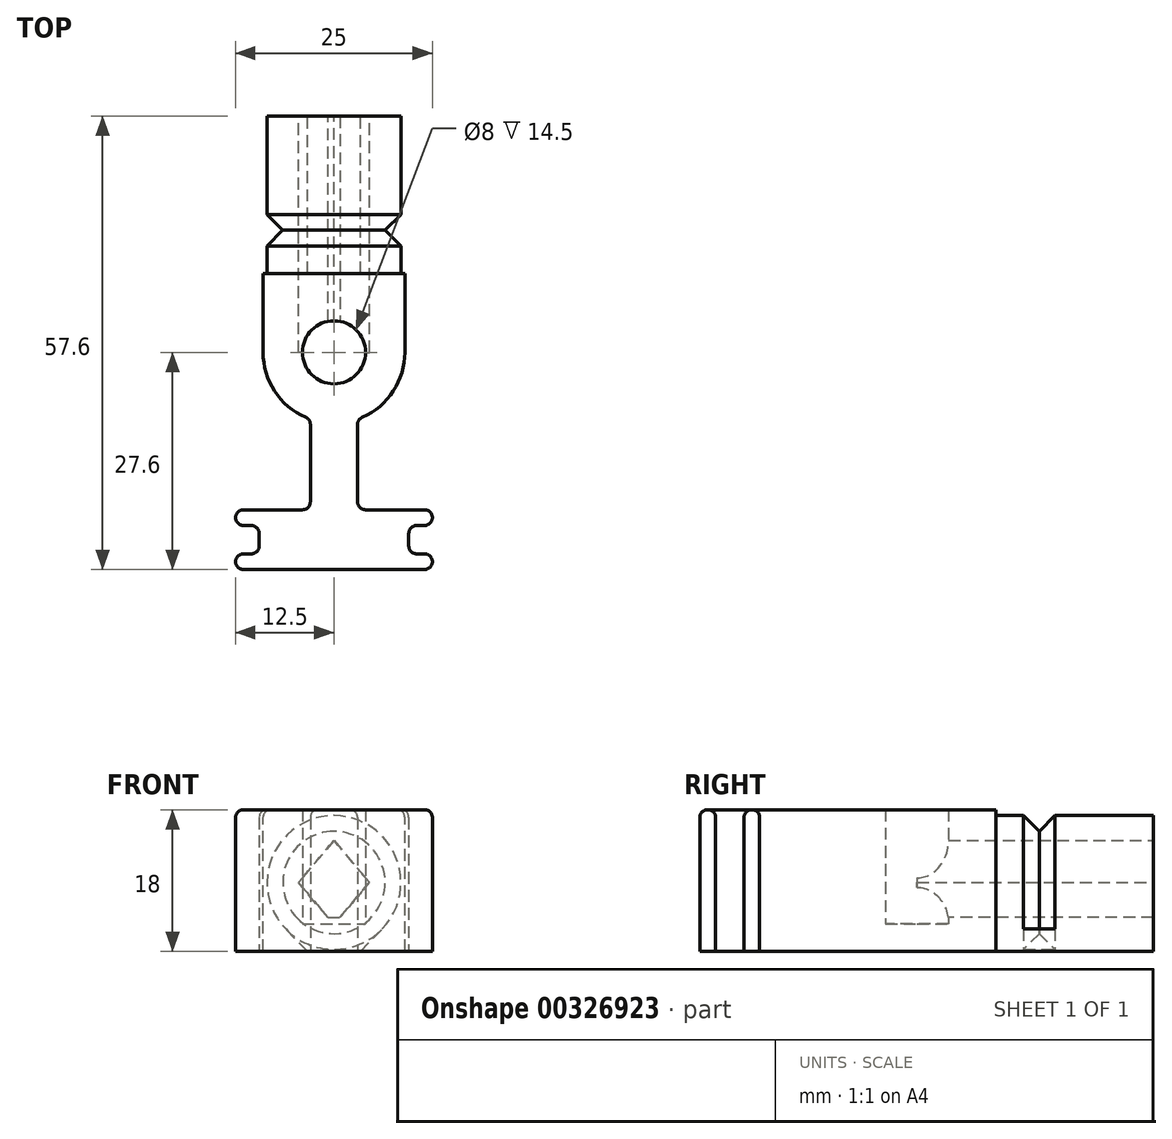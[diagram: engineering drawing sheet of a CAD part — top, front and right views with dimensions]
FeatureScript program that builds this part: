
annotation { "Feature Type Name" : "Feature", "Feature Type Description" : "" }
export const myFeature = defineFeature(function(context is Context, id is Id, definition is map)
    precondition{}
    {
        {
            var Q0;
            Q0=qCreatedBy(makeId("Top.planeOp"),FACE);
            var sketch = newSketch(context, id + "F0", { "sketchPlane" : qUnion([Q0])});
            skCircle(sketch, "E0", {"center": v(0, 0) * mm, "radius": 4 * mm});
            skArc(sketch, "E1", {"start": v(3, -8.49) * mm, "mid": v(7.35, -5.2) * mm, "end": v(9, 0) * mm});
            skLineSegment(sketch, "E2", {"start": v(-3, -8.49) * mm, "end": v(-3, -20) * mm});
            skLineSegment(sketch, "E3", {"start": v(-3, -20) * mm, "end": v(-12.5, -20) * mm});
            skLineSegment(sketch, "E4", {"start": v(-12.5, -20) * mm, "end": v(-12.5, -22) * mm});
            skLineSegment(sketch, "E5", {"start": v(-12.5, -22) * mm, "end": v(-9.5, -22) * mm});
            skLineSegment(sketch, "E6", {"start": v(-9.5, -22) * mm, "end": v(-9.5, -25.6) * mm});
            skLineSegment(sketch, "E7", {"start": v(-9.5, -25.6) * mm, "end": v(-12.5, -25.6) * mm});
            skLineSegment(sketch, "E8", {"start": v(-12.5, -25.6) * mm, "end": v(-12.5, -27.6) * mm});
            skLineSegment(sketch, "E9", {"start": v(-12.5, -27.6) * mm, "end": v(0, -27.6) * mm});
            skLineSegment(sketch, "E10", {"start": v(0, -27.6) * mm, "end": v(0, 0) * mm, "construction": true});
            skLineSegment(sketch, "E11.MirrorCS", {"start": v(3, -8.49) * mm, "end": v(3, -20) * mm});
            skLineSegment(sketch, "E12.MirrorCS", {"start": v(12.5, -25.6) * mm, "end": v(12.5, -27.6) * mm});
            skLineSegment(sketch, "E13.MirrorCS", {"start": v(12.5, -20) * mm, "end": v(12.5, -22) * mm});
            skLineSegment(sketch, "E14.MirrorCS", {"start": v(12.5, -27.6) * mm, "end": v(0, -27.6) * mm});
            skLineSegment(sketch, "E15.MirrorCS", {"start": v(3, -20) * mm, "end": v(12.5, -20) * mm});
            skLineSegment(sketch, "E16.MirrorCS", {"start": v(12.5, -22) * mm, "end": v(9.5, -22) * mm});
            skLineSegment(sketch, "E17.MirrorCS", {"start": v(9.5, -25.6) * mm, "end": v(12.5, -25.6) * mm});
            skLineSegment(sketch, "E18.MirrorCS", {"start": v(9.5, -22) * mm, "end": v(9.5, -25.6) * mm});
            skLineSegment(sketch, "E19", {"start": v(-9, 0) * mm, "end": v(-9, 30) * mm});
            skLineSegment(sketch, "E20", {"start": v(-9, 30) * mm, "end": v(9, 30) * mm});
            skLineSegment(sketch, "E21", {"start": v(9, 30) * mm, "end": v(9, 0) * mm});
            skArc(sketch, "E22.trimOffspring", {"start": v(-9, 0) * mm, "mid": v(-7.35, -5.2) * mm, "end": v(-3, -8.49) * mm});
            skSolve(sketch);
        }
        {
            var Q0;
            Q0=qSketchRegion(id+"F0",true);
            extrude(context, id + "F1", {"entities" : qUnion([Q0]), "depth" : 18 * mm});
        }
        {
            var Q0;
            Q0=makeQuery(id+"F1.opExtrude","CAP_FACE",FACE,{"disambiguationData":[OSD([sQuery(id+"F0.wireOp",EDGE,"E0"),sQuery(id+"F0.wireOp",EDGE,"E1"),sQuery(id+"F0.wireOp",EDGE,"E2"),sQuery(id+"F0.wireOp",EDGE,"E3"),sQuery(id+"F0.wireOp",EDGE,"E4"),sQuery(id+"F0.wireOp",EDGE,"E5"),sQuery(id+"F0.wireOp",EDGE,"E6"),sQuery(id+"F0.wireOp",EDGE,"E7"),sQuery(id+"F0.wireOp",EDGE,"E8"),sQuery(id+"F0.wireOp",EDGE,"E9"),sQuery(id+"F0.wireOp",EDGE,"E11.MirrorCS"),sQuery(id+"F0.wireOp",EDGE,"E12.MirrorCS"),sQuery(id+"F0.wireOp",EDGE,"E13.MirrorCS"),sQuery(id+"F0.wireOp",EDGE,"E14.MirrorCS"),sQuery(id+"F0.wireOp",EDGE,"E15.MirrorCS"),sQuery(id+"F0.wireOp",EDGE,"E16.MirrorCS"),sQuery(id+"F0.wireOp",EDGE,"E17.MirrorCS"),sQuery(id+"F0.wireOp",EDGE,"E18.MirrorCS")])],"isStart":false});
            var sketch = newSketch(context, id + "F2", { "sketchPlane" : qUnion([Q0])});
            skCircle(sketch, "E23.0", {"center": v(0, 0) * mm, "radius": 4 * mm});
            skCircle(sketch, "E24", {"center": v(0, 0) * mm, "radius": 9 * mm});
            skSolve(sketch);
        }
        {
            var Q0;
            Q0=makeQuery(id+"F1.opExtrude","SWEPT_EDGE",EDGE,{"disambiguationData":[OSD([sQuery(id+"F0.wireOp",EDGE,"E11.MirrorCS"),sQuery(id+"F0.wireOp",EDGE,"E15.MirrorCS")])]});
            var Q1;
            Q1=makeQuery(id+"F1.opExtrude","SWEPT_EDGE",EDGE,{"disambiguationData":[OSD([sQuery(id+"F0.wireOp",EDGE,"E2"),sQuery(id+"F0.wireOp",EDGE,"E3")])]});
            var Q2;
            Q2=makeQuery(id+"F1.opExtrude","SWEPT_EDGE",EDGE,{"disambiguationData":[OSD([sQuery(id+"F0.wireOp",EDGE,"E1"),sQuery(id+"F0.wireOp",EDGE,"E2")])]});
            var Q3;
            Q3=makeQuery(id+"F1.opExtrude","SWEPT_EDGE",EDGE,{"disambiguationData":[OSD([sQuery(id+"F0.wireOp",EDGE,"E1"),sQuery(id+"F0.wireOp",EDGE,"E11.MirrorCS")])]});
            var Q4;
            Q4=makeQuery(id+"F1.opExtrude","SWEPT_EDGE",EDGE,{"disambiguationData":[OSD([sQuery(id+"F0.wireOp",EDGE,"E12.MirrorCS"),sQuery(id+"F0.wireOp",EDGE,"E14.MirrorCS")])]});
            var Q5;
            Q5=makeQuery(id+"F1.opExtrude","SWEPT_EDGE",EDGE,{"disambiguationData":[OSD([sQuery(id+"F0.wireOp",EDGE,"E8"),sQuery(id+"F0.wireOp",EDGE,"E9")])]});
            var Q6;
            Q6=makeQuery(id+"F1.opExtrude","SWEPT_EDGE",EDGE,{"disambiguationData":[OSD([sQuery(id+"F0.wireOp",EDGE,"E6"),sQuery(id+"F0.wireOp",EDGE,"E7")])]});
            var Q7;
            Q7=makeQuery(id+"F1.opExtrude","SWEPT_EDGE",EDGE,{"disambiguationData":[OSD([sQuery(id+"F0.wireOp",EDGE,"E7"),sQuery(id+"F0.wireOp",EDGE,"E8")])]});
            var Q8;
            Q8=makeQuery(id+"F1.opExtrude","SWEPT_EDGE",EDGE,{"disambiguationData":[OSD([sQuery(id+"F0.wireOp",EDGE,"E5"),sQuery(id+"F0.wireOp",EDGE,"E6")])]});
            var Q9;
            Q9=makeQuery(id+"F1.opExtrude","SWEPT_EDGE",EDGE,{"disambiguationData":[OSD([sQuery(id+"F0.wireOp",EDGE,"E4"),sQuery(id+"F0.wireOp",EDGE,"E5")])]});
            var Q10;
            Q10=makeQuery(id+"F1.opExtrude","SWEPT_EDGE",EDGE,{"disambiguationData":[OSD([sQuery(id+"F0.wireOp",EDGE,"E3"),sQuery(id+"F0.wireOp",EDGE,"E4")])]});
            var Q11;
            Q11=makeQuery(id+"F1.opExtrude","SWEPT_EDGE",EDGE,{"disambiguationData":[OSD([sQuery(id+"F0.wireOp",EDGE,"E12.MirrorCS"),sQuery(id+"F0.wireOp",EDGE,"E17.MirrorCS")])]});
            var Q12;
            Q12=makeQuery(id+"F1.opExtrude","SWEPT_EDGE",EDGE,{"disambiguationData":[OSD([sQuery(id+"F0.wireOp",EDGE,"E17.MirrorCS"),sQuery(id+"F0.wireOp",EDGE,"E18.MirrorCS")])]});
            var Q13;
            Q13=makeQuery(id+"F1.opExtrude","SWEPT_EDGE",EDGE,{"disambiguationData":[OSD([sQuery(id+"F0.wireOp",EDGE,"E16.MirrorCS"),sQuery(id+"F0.wireOp",EDGE,"E18.MirrorCS")])]});
            var Q14;
            Q14=makeQuery(id+"F1.opExtrude","SWEPT_EDGE",EDGE,{"disambiguationData":[OSD([sQuery(id+"F0.wireOp",EDGE,"E13.MirrorCS"),sQuery(id+"F0.wireOp",EDGE,"E16.MirrorCS")])]});
            var Q15;
            Q15=makeQuery(id+"F1.opExtrude","SWEPT_EDGE",EDGE,{"disambiguationData":[OSD([sQuery(id+"F0.wireOp",EDGE,"E13.MirrorCS"),sQuery(id+"F0.wireOp",EDGE,"E15.MirrorCS")])]});
            fillet(context, id + "F3", {"entities" : qUnion([Q0, Q1, Q2, Q3, Q4, Q5, Q6, Q7, Q8, Q9, Q10, Q11, Q12, Q13, Q14, Q15]), "radius" : 1 * mm, "tangentPropagation" : true, "allowEdgeOverflow" : false});
        }
        {
            var Q0;
            Q0=makeQuery(id+"FmhpY0We5Ry6qRu_1.opFillet","BLEND_EDGE",EDGE,{"blendedFrom":[makeQuery(id+"FVQWmpm12YIfkNp_1.opExtrude","CAP_EDGE",EDGE,{"disambiguationData":[OSD([sQuery(id+"F2.wireOp",EDGE,"E24")])],"isStart":true}),makeQuery(id+"F1.opExtrude","SWEPT_FACE",FACE,{"disambiguationData":[OSD([sQuery(id+"F0.wireOp",EDGE,"E2")])]})],"blendedInto":[makeQuery(id+"F1.opExtrude","SWEPT_FACE",FACE,{"disambiguationData":[OSD([sQuery(id+"F0.wireOp",EDGE,"E2")])]})]});
            var Q1;
            Q1=makeQuery(id+"FmhpY0We5Ry6qRu_1.opFillet","BLEND_EDGE",EDGE,{"blendedFrom":[makeQuery(id+"FVQWmpm12YIfkNp_1.opExtrude","CAP_EDGE",EDGE,{"disambiguationData":[OSD([sQuery(id+"F2.wireOp",EDGE,"E24")])],"isStart":true}),makeQuery(id+"F3.opFillet","BLEND_FACE",FACE,{"disambiguationData":[OSD([sQuery(id+"F0.wireOp",EDGE,"E1"),sQuery(id+"F0.wireOp",EDGE,"E2")])]})],"blendedInto":[makeQuery(id+"F3.opFillet","BLEND_FACE",FACE,{"disambiguationData":[OSD([sQuery(id+"F0.wireOp",EDGE,"E1"),sQuery(id+"F0.wireOp",EDGE,"E2")])]})]});
            var Q2;
            Q2=makeQuery(id+"F1.opExtrude","CAP_EDGE",EDGE,{"disambiguationData":[OSD([sQuery(id+"F0.wireOp",EDGE,"E2")])],"isStart":false});
            fillet(context, id + "F4", {"entities" : qUnion([Q0, Q1, Q2]), "radius" : 1 * mm, "tangentPropagation" : true, "allowEdgeOverflow" : false});
        }
        {
            var Q0;
            Q0=makeQuery(id+"F1.opExtrude","SWEPT_FACE",FACE,{"disambiguationData":[OSD([sQuery(id+"F0.wireOp",EDGE,"E20")])]});
            var sketch = newSketch(context, id + "F5", { "sketchPlane" : qUnion([Q0])});
            skLineSegment(sketch, "E25", {"start": v(0, 0) * mm, "end": v(0, 27.76) * mm, "construction": true});
            skLineSegment(sketch, "E26", {"start": v(0, 0) * mm, "end": v(3.37, 0) * mm});
            skLineSegment(sketch, "E27", {"start": v(3.37, 0) * mm, "end": v(6.11, 2.84) * mm});
            skArc(sketch, "E28", {"start": v(6.11, 2.84) * mm, "mid": v(7.82, 12.06) * mm, "end": v(0, 17.24) * mm});
            skLineSegment(sketch, "E29.MirrorCS", {"start": v(-3.37, 0) * mm, "end": v(-6.11, 2.84) * mm});
            skLineSegment(sketch, "E30.MirrorCS", {"start": v(0, 0) * mm, "end": v(-3.37, 0) * mm});
            skArc(sketch, "E31.MirrorCS", {"start": v(-6.11, 2.84) * mm, "mid": v(-7.82, 12.06) * mm, "end": v(0, 17.24) * mm});
            skLineSegment(sketch, "E32.bottom", {"start": v(9, 0) * mm, "end": v(-11.14, 0) * mm});
            skLineSegment(sketch, "E32.top", {"start": v(9, 21.85) * mm, "end": v(-11.14, 21.85) * mm});
            skLineSegment(sketch, "E32.left", {"start": v(9, 0) * mm, "end": v(9, 21.85) * mm});
            skLineSegment(sketch, "E32.right", {"start": v(-11.14, 0) * mm, "end": v(-11.14, 21.85) * mm});
            skSolve(sketch);
        }
        {
            var Q0;
            {var subQ5=sQuery(id+"F5.wireOp",EDGE,"E32.top");Q0=makeQuery(id+"F5.imprint","IMPRINT",FACE,{"disambiguationData":[TD([[makeQuery(id+"F5.imprint","IMPRINT",EDGE,{"derivedFrom":subQ5}),1.0]])]});}
            var Q1;
            {var subQ9=sQuery(id+"F5.wireOp",EDGE,"E27");Q1=makeQuery(id+"F5.imprint","IMPRINT",FACE,{"disambiguationData":[TD([[makeQuery(id+"F5.imprint","IMPRINT",EDGE,{"derivedFrom":subQ9}),-1.0]])]});}
            extrude(context, id + "F6", {"entities" : qUnion([Q0, Q1]), "operationType" : NewBodyOperationType.REMOVE, "oppositeDirection" : true, "depth" : 20 * mm});
        }
        {
            var Q0;
            Q0=makeQuery(id+"F1.opExtrude","SWEPT_FACE",FACE,{"disambiguationData":[OSD([sQuery(id+"F0.wireOp",EDGE,"E20")])]});
            var sketch = newSketch(context, id + "F7", { "sketchPlane" : qUnion([Q0])});
            skLineSegment(sketch, "E33", {"start": v(0, 0) * mm, "end": v(0, 25.19) * mm, "construction": true});
            skArc(sketch, "E34.0", {"start": v(-6.11, 2.84) * mm, "mid": v(0, 17.24) * mm, "end": v(6.11, 2.84) * mm, "construction": true});
            skLineSegment(sketch, "E35", {"start": v(0, 14.1) * mm, "end": v(-4.5, 8.74) * mm});
            skLineSegment(sketch, "E36", {"start": v(0, 8.74) * mm, "end": v(-4.5, 8.74) * mm, "construction": true});
            skLineSegment(sketch, "E37.MirrorCS", {"start": v(0, 3.38) * mm, "end": v(-4.5, 8.74) * mm});
            skLineSegment(sketch, "E38.MirrorCS", {"start": v(0, 14.1) * mm, "end": v(4.5, 8.74) * mm});
            skLineSegment(sketch, "E39.MirrorCS", {"start": v(0, 3.38) * mm, "end": v(4.5, 8.74) * mm});
            skSolve(sketch);
        }
        {
            var Q0;
            Q0 = qSketchRegion(id + "F7", true);
            extrude(context, id + "F8", {"entities" : qUnion([Q0]), "operationType" : NewBodyOperationType.REMOVE, "oppositeDirection" : true, "depth" : 30 * mm});
        }
        {
            var Q0;
            Q0=makeQuery(id+"F8.boolean.opBoolean","COPY",EDGE,{"derivedFrom":makeQuery(id+"F8.opExtrude","SWEPT_EDGE",EDGE,{"disambiguationData":[OSD([sQuery(id+"F7.wireOp",EDGE,"E37.MirrorCS"),sQuery(id+"F7.wireOp",EDGE,"E39.MirrorCS")])]})});
            chamfer(context, id + "F9", {"entities" : qUnion([Q0]), "width" : 1 * mm, "tangentPropagation" : true});
        }
        {
            var Q0;
            Q0=makeQuery(id+"F1.opExtrude","CAP_FACE",FACE,{"disambiguationData":[OSD([sQuery(id+"F0.wireOp",EDGE,"E0"),sQuery(id+"F0.wireOp",EDGE,"E1"),sQuery(id+"F0.wireOp",EDGE,"E2"),sQuery(id+"F0.wireOp",EDGE,"E3"),sQuery(id+"F0.wireOp",EDGE,"E4"),sQuery(id+"F0.wireOp",EDGE,"E5"),sQuery(id+"F0.wireOp",EDGE,"E6"),sQuery(id+"F0.wireOp",EDGE,"E7"),sQuery(id+"F0.wireOp",EDGE,"E8"),sQuery(id+"F0.wireOp",EDGE,"E9"),sQuery(id+"F0.wireOp",EDGE,"E11.MirrorCS"),sQuery(id+"F0.wireOp",EDGE,"E12.MirrorCS"),sQuery(id+"F0.wireOp",EDGE,"E13.MirrorCS"),sQuery(id+"F0.wireOp",EDGE,"E14.MirrorCS"),sQuery(id+"F0.wireOp",EDGE,"E15.MirrorCS"),sQuery(id+"F0.wireOp",EDGE,"E16.MirrorCS"),sQuery(id+"F0.wireOp",EDGE,"E17.MirrorCS"),sQuery(id+"F0.wireOp",EDGE,"E18.MirrorCS"),sQuery(id+"F0.wireOp",EDGE,"E19"),sQuery(id+"F0.wireOp",EDGE,"E20"),sQuery(id+"F0.wireOp",EDGE,"E21"),sQuery(id+"F0.wireOp",EDGE,"E22.trimOffspring")])],"isStart":true});
            var sketch = newSketch(context, id + "F10", { "sketchPlane" : qUnion([Q0])});
            skCircle(sketch, "E40.0", {"center": v(0, 0) * mm, "radius": 4 * mm, "construction": true});
            skCircle(sketch, "E41", {"center": v(0, 0) * mm, "radius": 5 * mm});
            skSolve(sketch);
        }
        {
            var Q0;
            Q0 = qSketchRegion(id + "F10", true);
            extrude(context, id + "F11", {"entities" : qUnion([Q0]), "operationType" : NewBodyOperationType.ADD, "oppositeDirection" : true, "depth" : 3.5 * mm});
        }
        {
            var Q0;
            Q0=qCreatedBy(makeId("Right.planeOp"),FACE);
            var sketch = newSketch(context, id + "F12", { "sketchPlane" : qUnion([Q0])});
            skPoint(sketch, "E42.0", {"position": v(30, 17.24) * mm});
            skLineSegment(sketch, "E43", {"start": v(13.5, 17.24) * mm, "end": v(17.5, 17.24) * mm});
            skLineSegment(sketch, "E44", {"start": v(13.5, 17.24) * mm, "end": v(15.5, 15.24) * mm});
            skLineSegment(sketch, "E45", {"start": v(15.5, 15.24) * mm, "end": v(15.5, 17.24) * mm, "construction": true});
            skLineSegment(sketch, "E46.MirrorCS", {"start": v(17.5, 17.24) * mm, "end": v(15.5, 15.24) * mm});
            skSolve(sketch);
        }
        {
            var Q0;
            Q0 = qSketchRegion(id + "F12", true);
            var Q1;
            Q1=makeQuery(id+"F6.boolean.opBoolean","COPY",FACE,{"derivedFrom":makeQuery(id+"F6.opExtrude","SWEPT_FACE",FACE,{"disambiguationData":[OSD([sQuery(id+"F5.wireOp",EDGE,"E28"),sQuery(id+"F5.wireOp",EDGE,"E31.MirrorCS")])]})});
            revolve(context, id + "F13", {"operationType" : NewBodyOperationType.REMOVE, "entities" : qUnion([Q0]), "axis" : qUnion([Q1]), "revolveType" : RevolveType.FULL, "oppositeDirection" : true});
        }
    });
